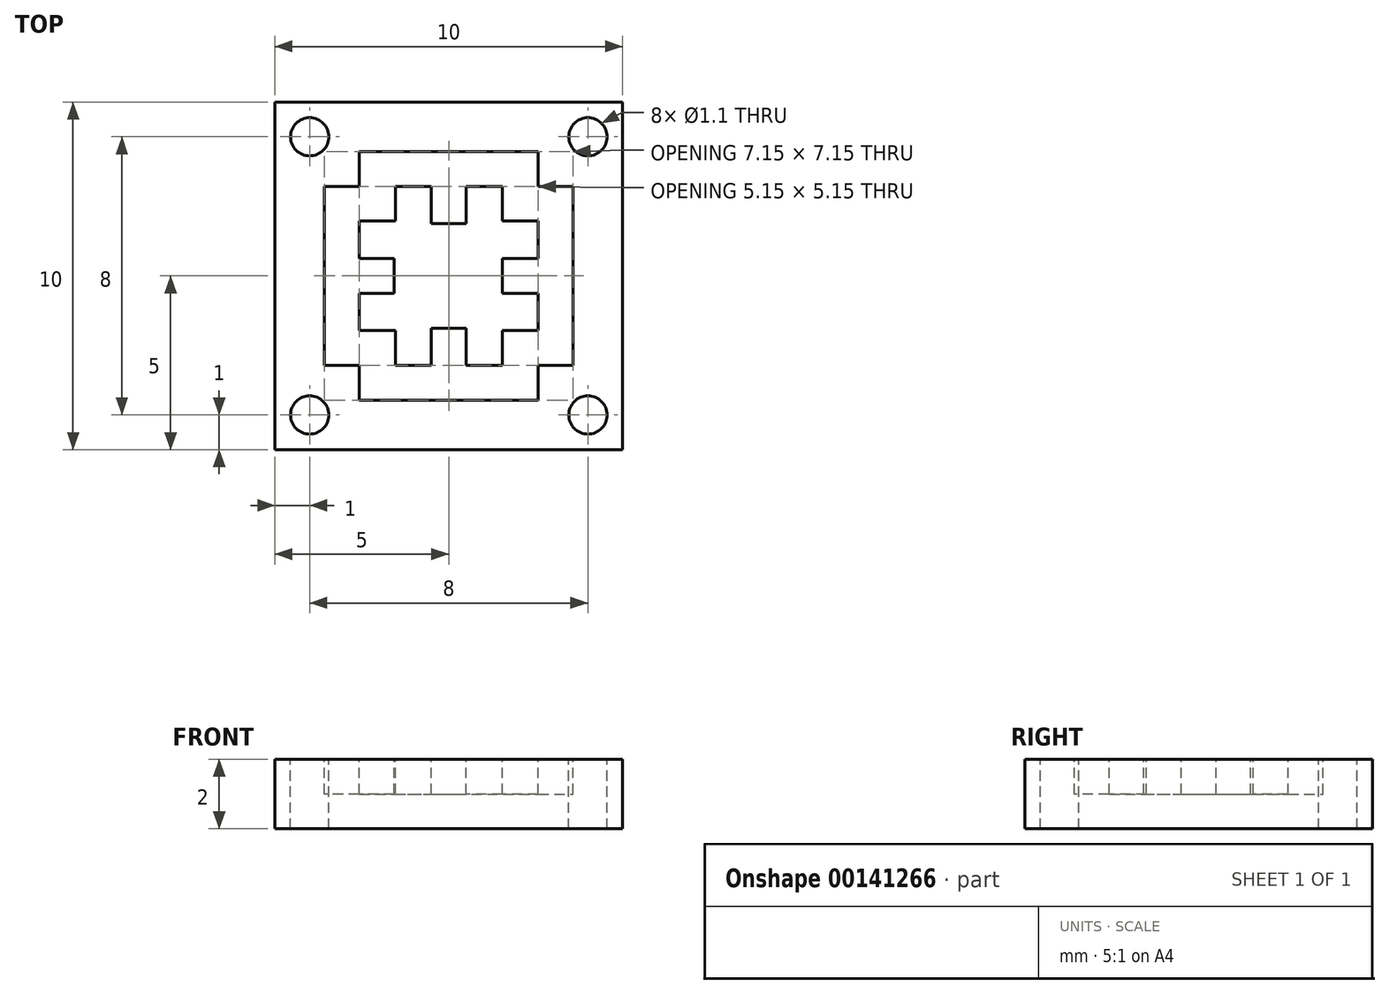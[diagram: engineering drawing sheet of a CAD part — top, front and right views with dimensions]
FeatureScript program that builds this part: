
annotation { "Feature Type Name" : "Feature", "Feature Type Description" : "" }
export const myFeature = defineFeature(function(context is Context, id is Id, definition is map)
    precondition{}
    {
        {
            var Q0;
            Q0=qCreatedBy(makeId("Top.planeOp"),FACE);
            var sketch = newSketch(context, id + "F0", { "sketchPlane" : qUnion([Q0])});
            skLineSegment(sketch, "E0.bottom", {"start": v(5, 5) * mm, "end": v(-5, 5) * mm});
            skLineSegment(sketch, "E0.top", {"start": v(5, -5) * mm, "end": v(-5, -5) * mm});
            skLineSegment(sketch, "E0.left", {"start": v(5, 5) * mm, "end": v(5, -5) * mm});
            skLineSegment(sketch, "E0.right", {"start": v(-5, 5) * mm, "end": v(-5, -5) * mm});
            skLineSegment(sketch, "E1.bottom", {"start": v(-2.58, -3.58) * mm, "end": v(2.58, -3.58) * mm});
            skLineSegment(sketch, "E1.top", {"start": v(-2.58, 3.58) * mm, "end": v(2.58, 3.58) * mm});
            skLineSegment(sketch, "E1.left", {"start": v(-3.58, -2.58) * mm, "end": v(-3.58, 2.58) * mm});
            skLineSegment(sketch, "E1.right", {"start": v(3.58, -2.58) * mm, "end": v(3.58, 2.58) * mm});
            skPoint(sketch, "E2", {"position": v(-2.58, -2.58) * mm});
            skLineSegment(sketch, "E3.bottom", {"start": v(-1.54, -2.58) * mm, "end": v(-0.5, -2.58) * mm});
            skLineSegment(sketch, "E3.left", {"start": v(-2.58, -1.58) * mm, "end": v(-2.58, -0.5) * mm});
            skLineSegment(sketch, "E4", {"start": v(-0.5, -1.5) * mm, "end": v(0.5, -1.5) * mm});
            skLineSegment(sketch, "E5", {"start": v(0.5, -1.5) * mm, "end": v(0.5, -2.58) * mm});
            skLineSegment(sketch, "E6", {"start": v(-0.5, -1.5) * mm, "end": v(-0.5, -2.58) * mm});
            skLineSegment(sketch, "E7.MirrorCS", {"start": v(-0.5, 1.5) * mm, "end": v(-0.5, 2.58) * mm});
            skLineSegment(sketch, "E8.MirrorCS", {"start": v(-0.5, 1.5) * mm, "end": v(0.5, 1.5) * mm});
            skLineSegment(sketch, "E9.MirrorCS", {"start": v(0.5, 1.5) * mm, "end": v(0.5, 2.58) * mm});
            skLineSegment(sketch, "E10", {"start": v(2.58, -0.5) * mm, "end": v(1.54, -0.5) * mm});
            skLineSegment(sketch, "E11", {"start": v(1.54, -0.5) * mm, "end": v(1.54, 0.5) * mm});
            skPoint(sketch, "E11.endSnap0", {"position": v(1.54, 0.5) * mm});
            skLineSegment(sketch, "E12", {"start": v(1.54, 0.5) * mm, "end": v(2.58, 0.5) * mm});
            skLineSegment(sketch, "E13.trimOffspring", {"start": v(0.5, 2.58) * mm, "end": v(1.54, 2.58) * mm});
            skLineSegment(sketch, "E14", {"start": v(-5, 0) * mm, "end": v(5, 0) * mm, "construction": true});
            skPoint(sketch, "E14.endSnap0", {"position": v(-5, 0) * mm});
            skLineSegment(sketch, "E15", {"start": v(0, 5) * mm, "end": v(0, -5) * mm, "construction": true});
            skPoint(sketch, "E15.endSnap0", {"position": v(0, -5) * mm});
            skCircle(sketch, "E16", {"center": v(-4, -4) * mm, "radius": 0.55 * mm});
            skCircle(sketch, "E17.MirrorC", {"center": v(4, -4) * mm, "radius": 0.55 * mm});
            skCircle(sketch, "E18.MirrorC", {"center": v(-4, 4) * mm, "radius": 0.55 * mm});
            skCircle(sketch, "E19.MirrorC", {"center": v(4, 4) * mm, "radius": 0.55 * mm});
            skLineSegment(sketch, "E20", {"start": v(-1.54, -2.58) * mm, "end": v(-1.54, -1.58) * mm});
            skLineSegment(sketch, "E21", {"start": v(-1.54, -1.58) * mm, "end": v(-2.58, -1.58) * mm});
            skLineSegment(sketch, "E22", {"start": v(-2.58, -2.58) * mm, "end": v(-2.58, -3.58) * mm});
            skLineSegment(sketch, "E23", {"start": v(-2.58, -2.58) * mm, "end": v(-3.58, -2.58) * mm});
            skLineSegment(sketch, "E24.MirrorCS", {"start": v(1.54, -2.58) * mm, "end": v(1.54, -1.58) * mm});
            skLineSegment(sketch, "E25.MirrorCS", {"start": v(1.54, -1.58) * mm, "end": v(2.58, -1.58) * mm});
            skLineSegment(sketch, "E26.MirrorCS", {"start": v(1.54, -2.58) * mm, "end": v(0.5, -2.58) * mm});
            skLineSegment(sketch, "E27.MirrorCS", {"start": v(2.58, -2.58) * mm, "end": v(2.58, -3.58) * mm});
            skLineSegment(sketch, "E28.MirrorCS", {"start": v(2.58, -2.58) * mm, "end": v(3.58, -2.58) * mm});
            skLineSegment(sketch, "E29", {"start": v(2.58, -1.58) * mm, "end": v(2.58, -0.5) * mm});
            skLineSegment(sketch, "E30.MirrorCS", {"start": v(-2.58, 2.58) * mm, "end": v(-3.58, 2.58) * mm});
            skLineSegment(sketch, "E31.MirrorCS", {"start": v(-2.58, 2.58) * mm, "end": v(-2.58, 3.58) * mm});
            skLineSegment(sketch, "E32.MirrorCS", {"start": v(-1.54, 2.58) * mm, "end": v(-1.54, 1.58) * mm});
            skLineSegment(sketch, "E33.MirrorCS", {"start": v(-1.54, 1.58) * mm, "end": v(-2.58, 1.58) * mm});
            skLineSegment(sketch, "E34.MirrorCS", {"start": v(-1.54, 2.58) * mm, "end": v(-0.5, 2.58) * mm});
            skLineSegment(sketch, "E35.MirrorCS", {"start": v(1.54, 2.58) * mm, "end": v(1.54, 1.58) * mm});
            skLineSegment(sketch, "E36.MirrorCS", {"start": v(1.54, 1.58) * mm, "end": v(2.58, 1.58) * mm});
            skLineSegment(sketch, "E37.MirrorCS", {"start": v(2.58, 2.58) * mm, "end": v(2.58, 3.58) * mm});
            skLineSegment(sketch, "E38.MirrorCS", {"start": v(2.58, 2.58) * mm, "end": v(3.58, 2.58) * mm});
            skLineSegment(sketch, "E39", {"start": v(2.58, 0.5) * mm, "end": v(2.58, 1.58) * mm});
            skLineSegment(sketch, "E40", {"start": v(-1.58, -0.5) * mm, "end": v(-2.58, -0.5) * mm});
            skLineSegment(sketch, "E41", {"start": v(-1.58, -0.5) * mm, "end": v(-1.58, 0.5) * mm});
            skLineSegment(sketch, "E42.trimOffspring", {"start": v(-1.58, 0.5) * mm, "end": v(-2.58, 0.5) * mm});
            skLineSegment(sketch, "E43.trimOffspring", {"start": v(-2.58, 0.5) * mm, "end": v(-2.58, 1.58) * mm});
            skSolve(sketch);
        }
        {
            var Q0;
            Q0=makeQuery(id+"F0.imprint","IMPRINT",FACE,{"disambiguationData":[TD([[makeQuery(id+"F0.imprint","IMPRINT",EDGE,{"derivedFrom":sQuery(id+"F0.wireOp",EDGE,"E0.bottom")}),1.0]])]});
            var Q1;
            Q1=makeQuery(id+"F0.imprint","IMPRINT",FACE,{"disambiguationData":[TD([[makeQuery(id+"F0.imprint","IMPRINT",EDGE,{"derivedFrom":sQuery(id+"F0.wireOp",EDGE,"E1.bottom")}),1.0]])]});
            var Q2;
            Q2=makeQuery(id+"F0.imprint","IMPRINT",FACE,{"disambiguationData":[TD([[makeQuery(id+"F0.imprint","IMPRINT",EDGE,{"derivedFrom":sQuery(id+"F0.wireOp",EDGE,"E3.bottom")}),1.0]])]});
            extrude(context, id + "F1", {"entities" : qUnion([Q0, Q1, Q2]), "oppositeDirection" : true, "depth" : 2 * mm});
        }
        {
            var Q0;
            Q0=makeQuery(id+"F0.imprint","IMPRINT",FACE,{"disambiguationData":[TD([[makeQuery(id+"F0.imprint","IMPRINT",EDGE,{"derivedFrom":sQuery(id+"F0.wireOp",EDGE,"E1.bottom")}),1.0]])]});
            extrude(context, id + "F2", {"entities" : qUnion([Q0]), "operationType" : NewBodyOperationType.REMOVE, "oppositeDirection" : true, "depth" : 1 * mm});
        }
    });
